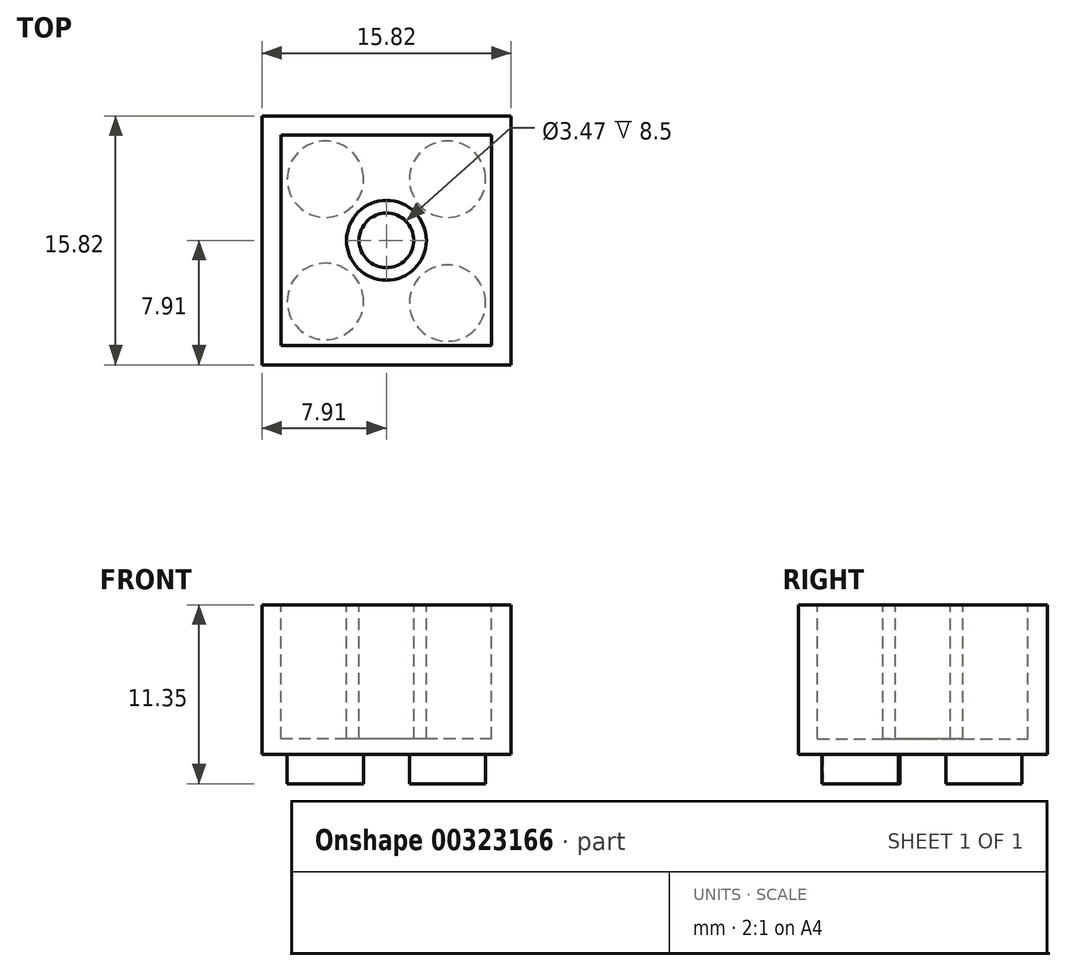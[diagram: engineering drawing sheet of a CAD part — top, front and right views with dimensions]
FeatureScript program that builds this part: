
annotation { "Feature Type Name" : "Feature", "Feature Type Description" : "" }
export const myFeature = defineFeature(function(context is Context, id is Id, definition is map)
    precondition{}
    {
        {
            var Q0;
            Q0=qCreatedBy(makeId("Top.planeOp"),FACE);
            var sketch = newSketch(context, id + "F0", { "sketchPlane" : qUnion([Q0])});
            skLineSegment(sketch, "E0.bottom", {"start": v(7.9, -7.9) * mm, "end": v(-7.9, -7.9) * mm});
            skLineSegment(sketch, "E0.top", {"start": v(7.9, 7.9) * mm, "end": v(-7.9, 7.9) * mm});
            skLineSegment(sketch, "E0.left", {"start": v(7.9, -7.9) * mm, "end": v(7.9, 7.9) * mm});
            skLineSegment(sketch, "E0.right", {"start": v(-7.9, -7.9) * mm, "end": v(-7.9, 7.9) * mm});
            skPoint(sketch, "E0.middle", {"position": v(0, 0) * mm});
            skCircle(sketch, "E1", {"center": v(-3.88, 3.88) * mm, "radius": 2.43 * mm});
            skCircle(sketch, "E2", {"center": v(3.88, 3.88) * mm, "radius": 2.43 * mm});
            skCircle(sketch, "E3", {"center": v(-3.88, -3.88) * mm, "radius": 2.43 * mm});
            skCircle(sketch, "E4", {"center": v(3.88, -3.98) * mm, "radius": 2.43 * mm});
            skSolve(sketch);
        }
        {
            var Q0;
            Q0=makeQuery(id+"F0.imprint","IMPRINT",FACE,{"disambiguationData":[TD([[makeQuery(id+"F0.imprint","IMPRINT",EDGE,{"derivedFrom":sQuery(id+"F0.wireOp",EDGE,"E0.bottom")}),-1.0]])]});
            var Q1;
            Q1=makeQuery(id+"F0.imprint","IMPRINT",FACE,{"disambiguationData":[TD([[makeQuery(id+"F0.imprint","IMPRINT",EDGE,{"derivedFrom":sQuery(id+"F0.wireOp",EDGE,"E1")}),1.0]])]});
            var Q2;
            Q2=makeQuery(id+"F0.imprint","IMPRINT",FACE,{"disambiguationData":[TD([[makeQuery(id+"F0.imprint","IMPRINT",EDGE,{"derivedFrom":sQuery(id+"F0.wireOp",EDGE,"E2")}),1.0]])]});
            var Q3;
            Q3=makeQuery(id+"F0.imprint","IMPRINT",FACE,{"disambiguationData":[TD([[makeQuery(id+"F0.imprint","IMPRINT",EDGE,{"derivedFrom":sQuery(id+"F0.wireOp",EDGE,"E4")}),1.0]])]});
            var Q4;
            Q4=makeQuery(id+"F0.imprint","IMPRINT",FACE,{"disambiguationData":[TD([[makeQuery(id+"F0.imprint","IMPRINT",EDGE,{"derivedFrom":sQuery(id+"F0.wireOp",EDGE,"E3")}),1.0]])]});
            extrude(context, id + "F1", {"entities" : qUnion([Q0, Q1, Q2, Q3, Q4]), "depth" : 9.5 * mm});
        }
        {
            var Q0;
            Q0=makeQuery(id+"F0.imprint","IMPRINT",FACE,{"disambiguationData":[TD([[makeQuery(id+"F0.imprint","IMPRINT",EDGE,{"derivedFrom":sQuery(id+"F0.wireOp",EDGE,"E3")}),1.0]])]});
            var Q1;
            Q1=makeQuery(id+"F0.imprint","IMPRINT",FACE,{"disambiguationData":[TD([[makeQuery(id+"F0.imprint","IMPRINT",EDGE,{"derivedFrom":sQuery(id+"F0.wireOp",EDGE,"E4")}),1.0]])]});
            var Q2;
            Q2=makeQuery(id+"F0.imprint","IMPRINT",FACE,{"disambiguationData":[TD([[makeQuery(id+"F0.imprint","IMPRINT",EDGE,{"derivedFrom":sQuery(id+"F0.wireOp",EDGE,"E2")}),1.0]])]});
            var Q3;
            Q3=makeQuery(id+"F0.imprint","IMPRINT",FACE,{"disambiguationData":[TD([[makeQuery(id+"F0.imprint","IMPRINT",EDGE,{"derivedFrom":sQuery(id+"F0.wireOp",EDGE,"E1")}),1.0]])]});
            extrude(context, id + "F2", {"entities" : qUnion([Q0, Q1, Q2, Q3]), "operationType" : NewBodyOperationType.ADD, "oppositeDirection" : true, "depth" : 1.85 * mm});
        }
        {
            var Q0;
            Q0=makeQuery(id+"F1.opExtrude","CAP_FACE",FACE,{"disambiguationData":[OSD([sQuery(id+"F0.wireOp",EDGE,"E0.bottom"),sQuery(id+"F0.wireOp",EDGE,"E0.top"),sQuery(id+"F0.wireOp",EDGE,"E0.left"),sQuery(id+"F0.wireOp",EDGE,"E0.right")])],"isStart":false});
            var sketch = newSketch(context, id + "F3", { "sketchPlane" : qUnion([Q0])});
            skCircle(sketch, "E5", {"center": v(0, 0) * mm, "radius": 2.54 * mm});
            skSolve(sketch);
        }
        {
            var Q0;
            Q0=makeQuery(id+"F3.imprint","IMPRINT",FACE,{"disambiguationData":[TD([[makeQuery(id+"F3.imprint","IMPRINT",EDGE,{"derivedFrom":sQuery(id+"F3.wireOp",EDGE,"E5")}),-1.0]])]});
            var sketch = newSketch(context, id + "F4", { "sketchPlane" : qUnion([Q0])});
            skLineSegment(sketch, "E6.bottom", {"start": v(6.69, -6.68) * mm, "end": v(-6.69, -6.69) * mm});
            skLineSegment(sketch, "E6.top", {"start": v(6.69, 6.69) * mm, "end": v(-6.69, 6.68) * mm});
            skLineSegment(sketch, "E6.left", {"start": v(6.69, -6.69) * mm, "end": v(6.69, 6.69) * mm});
            skLineSegment(sketch, "E6.right", {"start": v(-6.69, -6.69) * mm, "end": v(-6.69, 6.69) * mm});
            skPoint(sketch, "E6.middle", {"position": v(0, 0) * mm});
            skSolve(sketch);
        }
        {
            var Q0;
            Q0=makeQuery(id+"F4.imprint","IMPRINT",FACE,{"disambiguationData":[TD([[makeQuery(id+"F4.imprint","IMPRINT",EDGE,{"derivedFrom":sQuery(id+"F4.wireOp",EDGE,"E6.bottom")}),-1.0]])]});
            extrude(context, id + "F5", {"entities" : qUnion([Q0]), "operationType" : NewBodyOperationType.REMOVE, "oppositeDirection" : true, "depth" : 8.5 * mm});
        }
        {
            var Q0;
            Q0=makeQuery(id+"F3.imprint","IMPRINT",FACE,{"disambiguationData":[TD([[makeQuery(id+"F3.imprint","IMPRINT",EDGE,{"derivedFrom":sQuery(id+"F3.wireOp",EDGE,"E5")}),1.0]])]});
            var sketch = newSketch(context, id + "F6", { "sketchPlane" : qUnion([Q0])});
            skCircle(sketch, "E7", {"center": v(0, 0) * mm, "radius": 1.74 * mm});
            skSolve(sketch);
        }
        {
            var Q0;
            Q0=makeQuery(id+"F6.imprint","IMPRINT",FACE,{"disambiguationData":[TD([[makeQuery(id+"F6.imprint","IMPRINT",EDGE,{"derivedFrom":sQuery(id+"F6.wireOp",EDGE,"E7")}),1.0]])]});
            extrude(context, id + "F7", {"entities" : qUnion([Q0]), "operationType" : NewBodyOperationType.ADD, "oppositeDirection" : true, "depth" : 8.5 * mm});
        }
        {
            var Q0;
            Q0=makeQuery(id+"F6.imprint","IMPRINT",FACE,{"disambiguationData":[TD([[makeQuery(id+"F6.imprint","IMPRINT",EDGE,{"derivedFrom":sQuery(id+"F6.wireOp",EDGE,"E7")}),1.0]])]});
            var Q1;
            Q1=sQuery(id+"F6.wireOp",EDGE,"E7");
            extrude(context, id + "F8", {"entities" : qUnion([Q0]), "operationType" : NewBodyOperationType.REMOVE, "surfaceEntities" : qUnion([Q1]), "oppositeDirection" : true, "depth" : 8.5 * mm});
        }
    });
